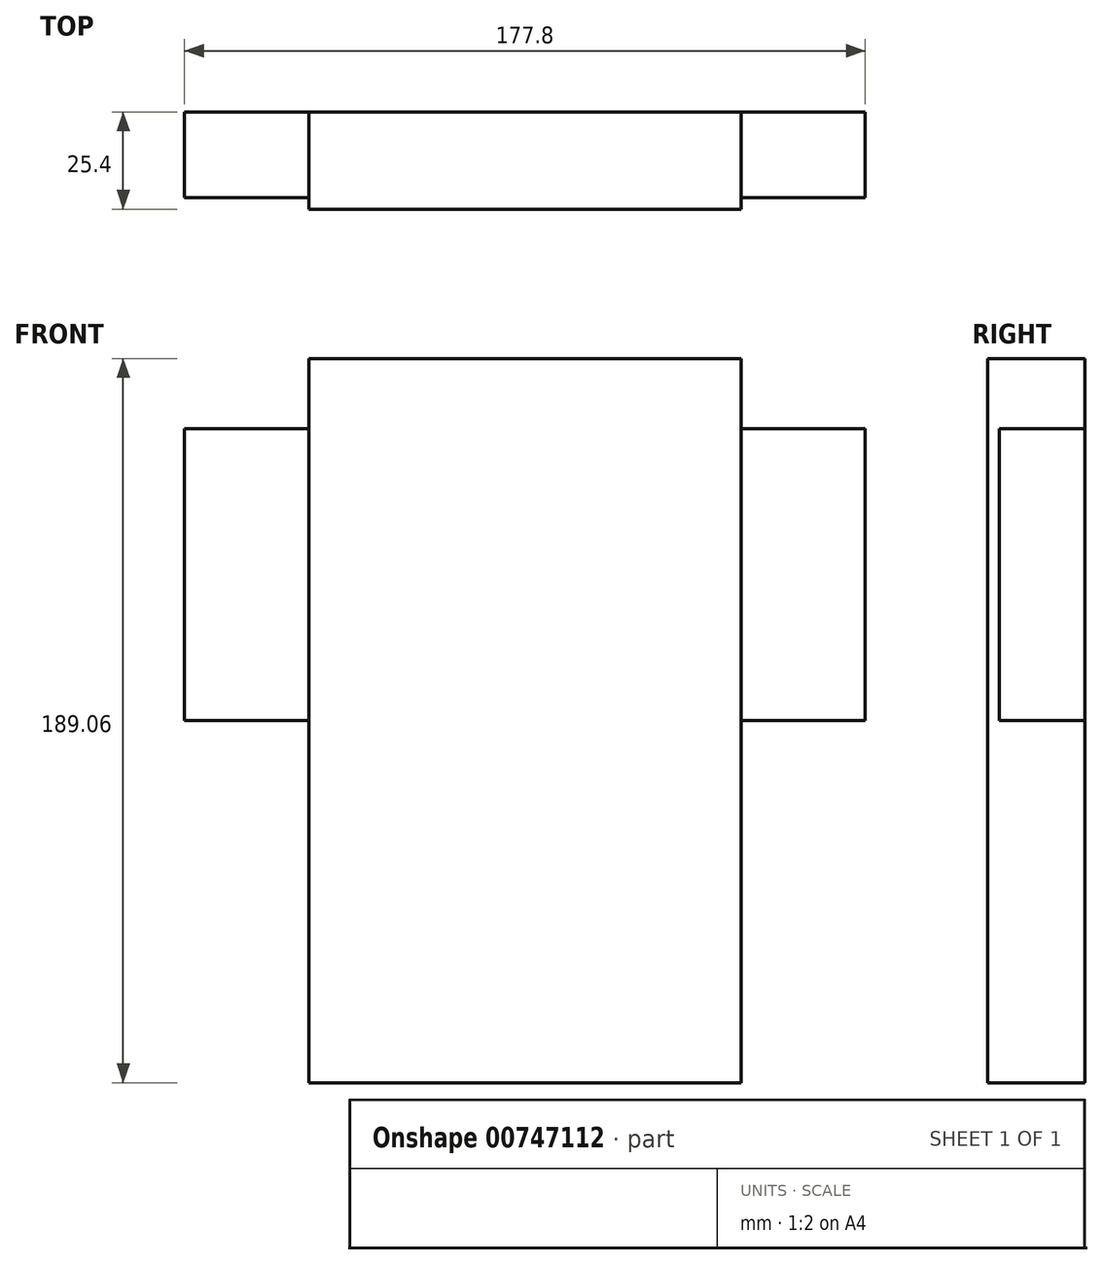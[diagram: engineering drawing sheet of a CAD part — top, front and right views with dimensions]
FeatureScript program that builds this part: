
annotation { "Feature Type Name" : "Feature", "Feature Type Description" : "" }
export const myFeature = defineFeature(function(context is Context, id is Id, definition is map)
    precondition{}
    {
        {
            var Q0;
            Q0=qCreatedBy(makeId("Front.planeOp"),FACE);
            var sketch = newSketch(context, id + "F0", { "sketchPlane" : qUnion([Q0])});
            skLineSegment(sketch, "E0.bottom", {"start": v(88.9, 38.1) * mm, "end": v(-88.9, 38.1) * mm});
            skLineSegment(sketch, "E0.top", {"start": v(88.9, -38.1) * mm, "end": v(-88.9, -38.1) * mm});
            skLineSegment(sketch, "E0.left", {"start": v(88.9, 38.1) * mm, "end": v(88.9, -38.1) * mm});
            skLineSegment(sketch, "E0.right", {"start": v(-88.9, 38.1) * mm, "end": v(-88.9, -38.1) * mm});
            skPoint(sketch, "E0.middle", {"position": v(0, 0) * mm});
            skSolve(sketch);
        }
        {
            var Q0;
            Q0=makeQuery(id+"F0.imprint","IMPRINT",FACE,{"disambiguationData":[TD([[makeQuery(id+"F0.imprint","IMPRINT",EDGE,{"derivedFrom":sQuery(id+"F0.wireOp",EDGE,"E0.bottom")}),1.0]])]});
            extrude(context, id + "F1", {"entities" : qUnion([Q0]), "depth" : 22.43 * mm, "offsetDistance" : 25.4 * mm});
        }
        {
            var Q0;
            Q0=qCreatedBy(makeId("Front.planeOp"),FACE);
            var sketch = newSketch(context, id + "F2", { "sketchPlane" : qUnion([Q0])});
            skLineSegment(sketch, "E1.bottom", {"start": v(56.46, -132.68) * mm, "end": v(-56.46, -132.68) * mm});
            skLineSegment(sketch, "E1.top", {"start": v(56.46, 56.38) * mm, "end": v(-56.46, 56.38) * mm});
            skLineSegment(sketch, "E1.left", {"start": v(56.46, -132.68) * mm, "end": v(56.46, 56.38) * mm});
            skLineSegment(sketch, "E1.right", {"start": v(-56.46, -132.68) * mm, "end": v(-56.46, 56.38) * mm});
            skPoint(sketch, "E1.middle", {"position": v(0, -38.15) * mm});
            skSolve(sketch);
        }
        {
            var Q0;
            Q0 = qSketchRegion(id + "F2", true);
            extrude(context, id + "F3", {"entities" : qUnion([Q0]), "operationType" : NewBodyOperationType.ADD, "depth" : 25.4 * mm, "offsetDistance" : 25.4 * mm});
        }
    });
